# Revit family: 306_H7_X_-S_
name_source: partatom
category: Pipe Accessories
units: mm (PartAtom-declared; Revit-internal decimal feet)

## family parameters
Always vertical = Yes
Cut with Voids When Loaded = No
Part Type = Valve - Breaks Into
Round Connector Dimension = Use Diameter
Shared = No
Work Plane-Based = No

## types (9) — shared parameters
CAT0 = Yes
Description = Globe valve, 3-way, Flange, PN 25
L2D_Min = 3048 mm
Manufacturer = Belimo
QmdConnectorList = 301;D;302;D;303;D
magiPartTypeId = 306
magiProductFamilyId = H7*X*-S*
zero-valued in all types: MC_Default_elevation

## per-type parameters (varying)
| type | B | C | C__ve | D | DD1 | DD2 | DR | FD | HH | HH1 | HH1__ve | HH2 | HH3 | HH4 | HH4__ve | HH5 | L2 | L2D | L4 | L42 | LL1 | LM | W2D | ZZ |
| H7015X4-S2 | 65 mm | 16 mm  [stored 0.0524934 ft] | -16 mm  [stored -0.0524934 ft] | 15 mm | 34 mm | 48 mm | 24 mm  [stored 0.0787402 ft] | 96 mm | 69 mm | 17 mm | -17 mm | 34 mm | 52 mm | 49 mm | -49 mm  [stored -0.160761 ft] | 17 mm | 65 mm | 130 mm | 33 mm | 26 mm | 43 mm | 98 mm | 15 mm  [stored 0.0492126 ft] | 52 mm |
| H7100X160-S4 | 150 mm | 24 mm  [stored 0.0787402 ft] | -24 mm  [stored -0.0787402 ft] | 100 mm | 82 mm | 118 mm | 59 mm | 235 mm | 106 mm | 27 mm | -27 mm | 53 mm | 80 mm | 126 mm | -126 mm  [stored -0.413386 ft] | 27 mm | 175 mm | 350 mm | 88 mm | 65 mm | 103 mm | 302 mm | 100 mm | 80 mm |
| H7080X100-S4 | 130 mm | 24 mm  [stored 0.0787402 ft] | -24 mm  [stored -0.0787402 ft] | 80 mm | 70 mm | 100 mm | 50 mm | 200 mm | 98 mm | 25 mm  [stored 0.082021 ft] | -25 mm | 49 mm | 74 mm | 106 mm | -106 mm  [stored -0.347769 ft] | 25 mm  [stored 0.082021 ft] | 155 mm | 310 mm | 78 mm | 55 mm | 93 mm | 262 mm | 80 mm | 74 mm |
| H7065X63-S4 | 120 mm | 22 mm  [stored 0.0721785 ft] | -22 mm  [stored -0.0721785 ft] | 65 mm | 65 mm | 93 mm | 46 mm | 185 mm | 92 mm | 23 mm  [stored 0.0754593 ft] | -23 mm  [stored -0.0754593 ft] | 46 mm | 69 mm | 98 mm | -98 mm  [stored -0.321522 ft] | 23 mm  [stored 0.0754593 ft] | 145 mm | 290 mm | 73 mm | 51 mm | 88 mm | 246 mm | 65 mm | 69 mm |
| H7050X40-S2 | 100 mm | 20 mm  [stored 0.0656168 ft] | -20 mm  [stored -0.0656168 ft] | 50 mm | 58 mm | 83 mm | 41 mm | 165 mm | 82 mm | 21 mm | -21 mm | 41 mm | 62 mm | 80 mm | -80 mm  [stored -0.262467 ft] | 21 mm | 115 mm | 230 mm | 58 mm | 45 mm | 73 mm | 190 mm | 50 mm | 61 mm |
| H7040X25-S2 | 90 mm | 18 mm  [stored 0.0590551 ft] | -18 mm  [stored -0.0590551 ft] | 40 mm | 53 mm | 75 mm | 38 mm | 150 mm | 83 mm | 21 mm | -21 mm | 41 mm | 62 mm | 72 mm | -72 mm  [stored -0.23622 ft] | 21 mm | 100 mm | 200 mm | 50 mm | 41 mm | 65 mm | 164 mm | 40 mm | 62 mm |
| H7032X16-S2 | 80 mm | 18 mm  [stored 0.0590551 ft] | -18 mm  [stored -0.0590551 ft] | 32 mm | 49 mm | 70 mm | 35 mm  [stored 0.114829 ft] | 140 mm | 81 mm | 20 mm  [stored 0.0656168 ft] | -20 mm  [stored -0.0656168 ft] | 40 mm | 61 mm | 62 mm | -62 mm  [stored -0.203412 ft] | 20 mm  [stored 0.0656168 ft] | 90 mm | 180 mm | 45 mm | 39 mm | 60 mm | 144 mm | 32 mm  [stored 0.104987 ft] | 61 mm |
| H7025X10-S2 | 75 mm | 18 mm  [stored 0.0590551 ft] | -18 mm  [stored -0.0590551 ft] | 25 mm | 40 mm | 58 mm | 29 mm | 115 mm | 70 mm | 18 mm  [stored 0.0590551 ft] | -18 mm  [stored -0.0590551 ft] | 35 mm  [stored 0.114829 ft] | 53 mm | 57 mm | -57 mm  [stored -0.187008 ft] | 18 mm  [stored 0.0590551 ft] | 80 mm | 160 mm | 40 mm | 32 mm  [stored 0.104987 ft] | 50 mm | 124 mm | 25 mm  [stored 0.082021 ft] | 53 mm |
| H7020X6P3-S2 | 70 mm | 18 mm  [stored 0.0590551 ft] | -18 mm  [stored -0.0590551 ft] | 20 mm | 37 mm | 53 mm | 26 mm | 105 mm | 69 mm | 17 mm | -17 mm | 34 mm | 52 mm | 52 mm | -52 mm  [stored -0.170604 ft] | 17 mm | 75 mm | 150 mm | 38 mm | 29 mm | 48 mm | 114 mm | 20 mm  [stored 0.0656168 ft] | 52 mm |

note: column(s) folded — value = type name in every type: magiProductCode, magiProductId

note: [stored X ft] marks values corroborated as IEEE doubles in the binary element streams (Revit-internal decimal feet)

## geometry (parser evidence)
native form markers: Sweep x2
no freeform markers — native parametric forms only
